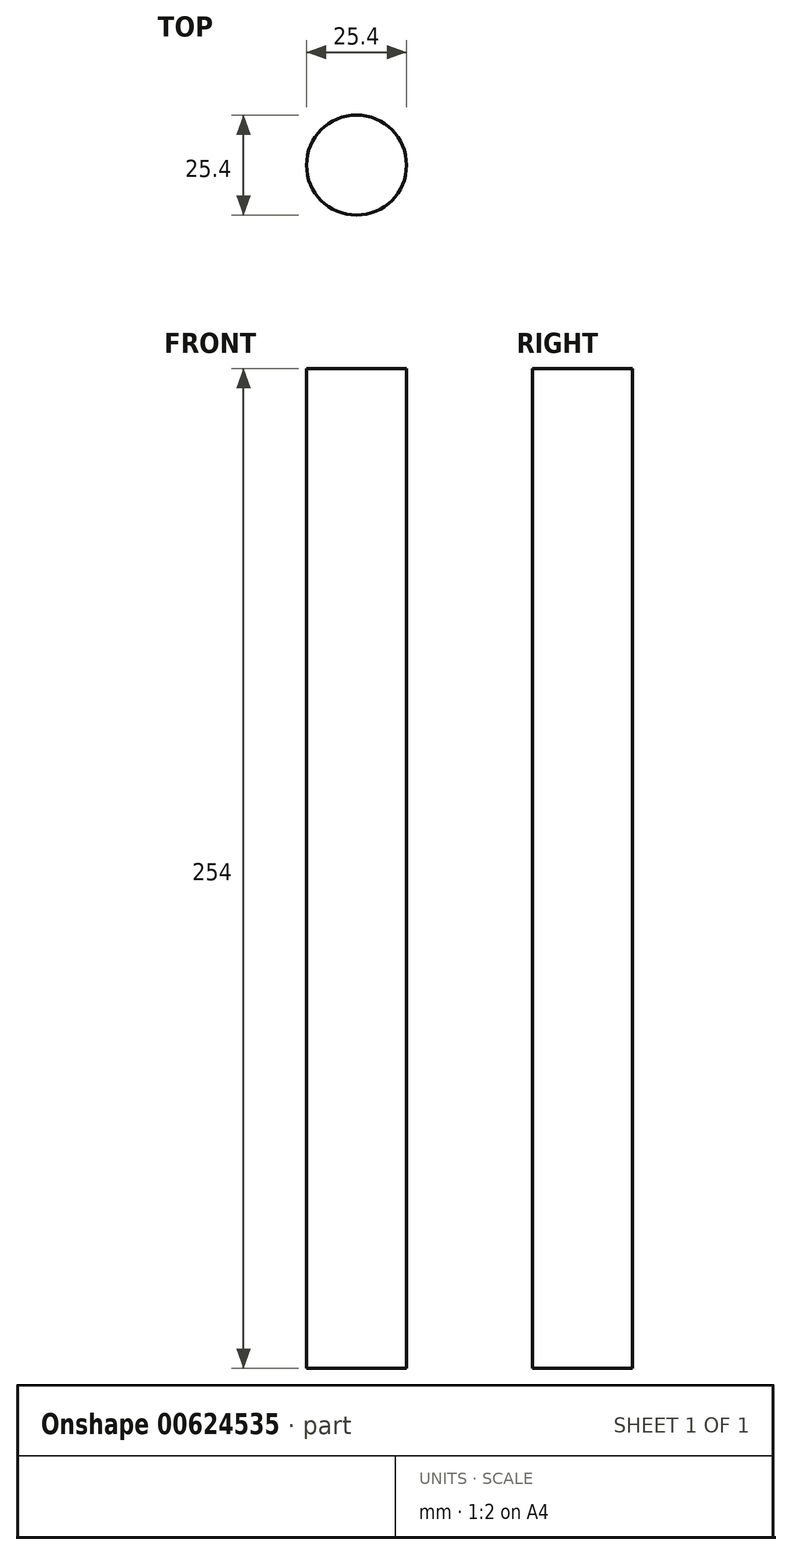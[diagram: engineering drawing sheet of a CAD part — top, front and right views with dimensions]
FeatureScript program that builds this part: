
annotation { "Feature Type Name" : "Feature", "Feature Type Description" : "" }
export const myFeature = defineFeature(function(context is Context, id is Id, definition is map)
    precondition{}
    {
        {
            var Q0;
            Q0=qCreatedBy(makeId("Top.planeOp"),FACE);
            var sketch = newSketch(context, id + "F0", { "sketchPlane" : qUnion([Q0])});
            skCircle(sketch, "E0", {"center": v(0, 0) * mm, "radius": 12.7 * mm});
            skSolve(sketch);
        }
        {
            var Q0;
            Q0=makeQuery(id+"F0.imprint","IMPRINT",FACE,{"disambiguationData":[TD([[makeQuery(id+"F0.imprint","IMPRINT",EDGE,{"derivedFrom":sQuery(id+"F0.wireOp",EDGE,"E0")}),1.0]])]});
            extrude(context, id + "F1", {"entities" : qUnion([Q0]), "oppositeDirection" : true, "depth" : 254 * mm, "offsetDistance" : 25.4 * mm});
        }
    });
